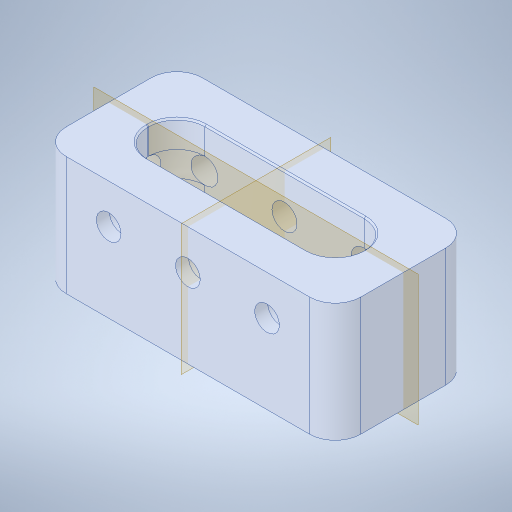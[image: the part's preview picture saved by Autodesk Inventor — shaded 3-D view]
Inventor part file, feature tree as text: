
AUTODESK INVENTOR PART (.ipt)
format: ipt  version: 2023.4 (Build 274418000, 418)  size: 422,400 bytes
history: native  units: in
note: dims shown in document units (in); Inventor stores cm internally (conversion verified against a paired STEP export)
features: sketch x2, projected_geometry x2, extrude x1, hole x1, chamfer x1
ambient origin geometry x8: Origin, YZ Plane, XZ Plane, XY Plane, X Axis, Y Axis, Z Axis, Center Point
bodies: Solid1 (feature_tree)
feature tree (7):
  extrude  "Extrusion1"  Depth=1.0in TaperAngle=0.0deg
  hole  "Hole1"  [1 undecoded]
  sketch  "Sketch1"  dims[d0=0.0625in d1=1.0in d2=0.0in]
  projected_geometry  "Projected Loop1"
  sketch  "Sketch2"  dims[d3=0.156in d4=0.38in d5=0.385in d6=0.25in d7=0.563in d8=1.0in d9=0.8108in]
  projected_geometry  "Projected Loop2"
  chamfer  "Chamfer2"  [1 undecoded]
note: 2 required parameter values undecoded (feature->parameter linkage not recoverable at this tier; creation-order binding heuristic only, values carry confidence <= 0.55)
